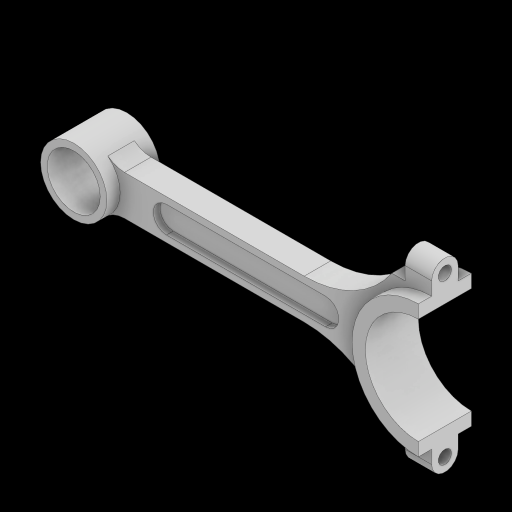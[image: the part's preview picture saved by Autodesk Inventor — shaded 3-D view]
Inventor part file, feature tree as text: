
AUTODESK INVENTOR PART (.ipt)
format: ipt  version: 2024 (Build 280153000, 153)  size: 208,896 bytes
history: native  units: in
note: dims shown in document units (in); Inventor stores cm internally (conversion verified against a paired STEP export)
features: sketch x3, extrude x3, fillet x2, mirror x2, hole x1
ambient origin geometry x8: Origin, YZ Plane, XZ Plane, XY Plane, X Axis, Y Axis, Z Axis, Center Point
bodies: Solid1 (feature_tree)
feature tree (11):
  sketch  "Sketch1"  dims[d0=2.0in d1=1.25in]
  extrude  "CENTER WEB"  Depth=1.25in
  extrude  "END RINGS"  Depth=1.0in
  fillet  "Fillet1"  Radius=2.5in
  fillet  "Fillet2"  Radius=0.75in
  hole  "Hole1"  [1 undecoded]
  mirror  "Mirror1"
  extrude  "RIGHT POCKET"  Depth=0.5in
  mirror  "Mirror2"
  sketch  "Sketch2"  dims[d2=6.5in d3=1.0in d4=2.5in d5=0.75in]
  sketch  "Sketch3"  dims[d6=0.375in d7=1.75in d8=0.5in d10=0.75in d11=1.25in d12=4.0in d14=0.5in d15=0.0in d16=1.0in d17=0.0in d18=0.5in d19=0.25in d20=0.25in d21=0.75in d22=0.375in d23=0.25in d24=0.5635in d25=1.0in d26=0.8108in d27=0.25in d28=3.0in d29=2.0in d30=0.25in d31=0.125in d32=0.0in]
note: 1 required parameter value undecoded (feature->parameter linkage not recoverable at this tier; creation-order binding heuristic only, values carry confidence <= 0.55)
